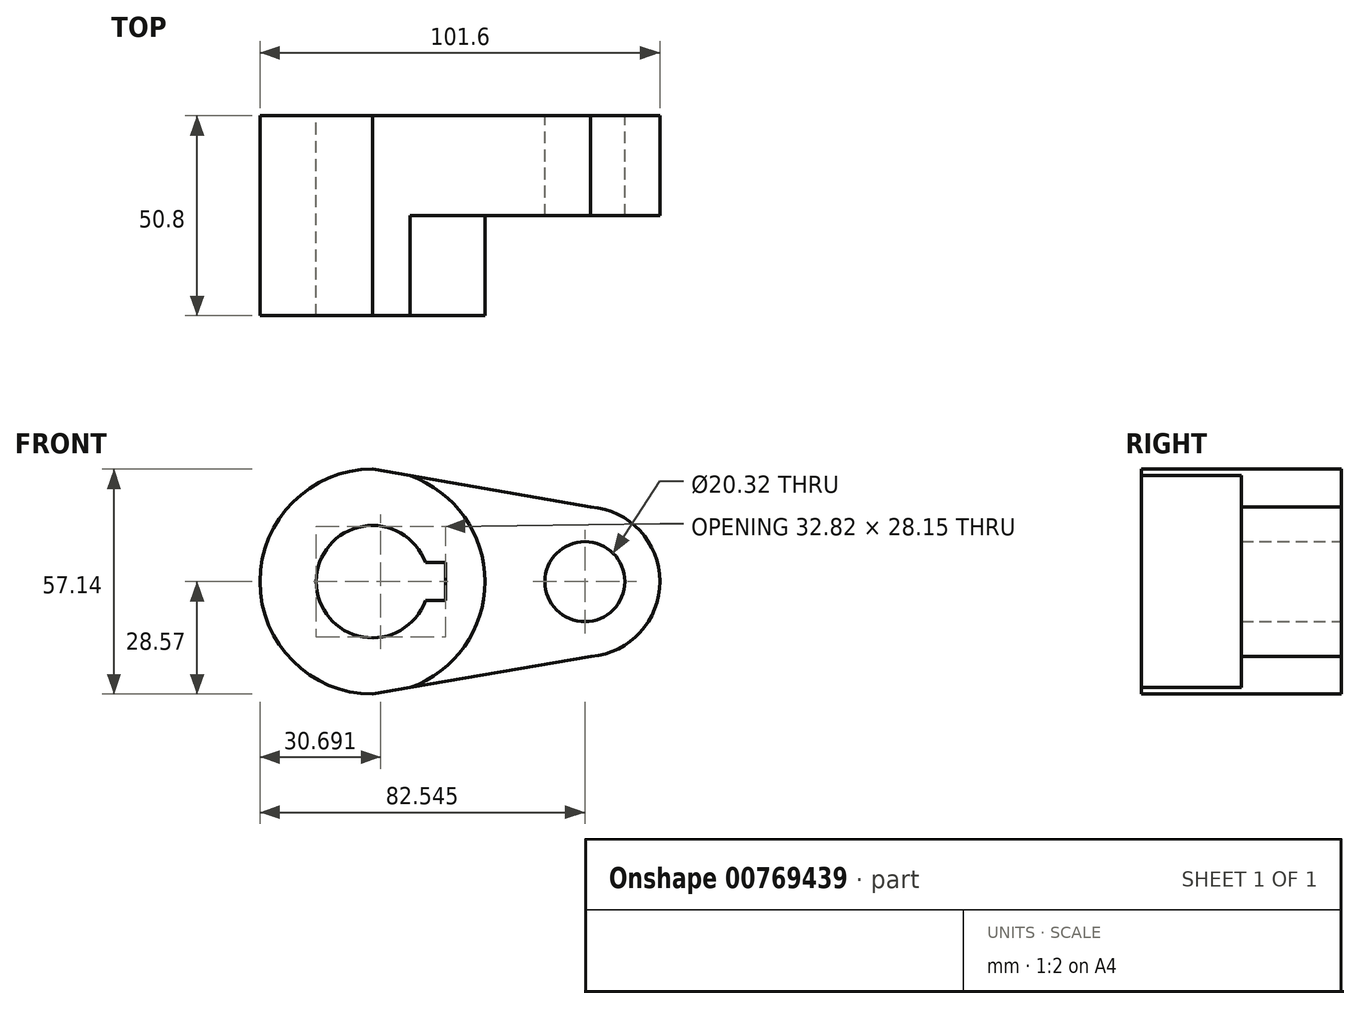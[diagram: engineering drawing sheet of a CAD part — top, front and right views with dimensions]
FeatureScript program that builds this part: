
annotation { "Feature Type Name" : "Feature", "Feature Type Description" : "" }
export const myFeature = defineFeature(function(context is Context, id is Id, definition is map)
    precondition{}
    {
        {
            var Q0;
            Q0=qCreatedBy(makeId("Front.planeOp"),FACE);
            var sketch = newSketch(context, id + "F0", { "sketchPlane" : qUnion([Q0])});
            skArc(sketch, "E0", {"start": v(0, 28.58) * mm, "mid": v(-28.58, 0) * mm, "end": v(0, -28.58) * mm});
            skArc(sketch, "E1", {"start": v(13.45, 4.83) * mm, "mid": v(-14.29, 0) * mm, "end": v(13.45, -4.83) * mm});
            skLineSegment(sketch, "E2.bottom", {"start": v(13.45, -4.83) * mm, "end": v(18.53, -4.83) * mm});
            skLineSegment(sketch, "E2.top", {"start": v(13.45, 4.83) * mm, "end": v(18.53, 4.83) * mm});
            skLineSegment(sketch, "E2.left", {"start": v(0, -4.83) * mm, "end": v(0, 0) * mm});
            skLineSegment(sketch, "E2.right", {"start": v(18.53, -4.83) * mm, "end": v(18.53, 4.83) * mm});
            skCircle(sketch, "E3", {"center": v(53.98, 0) * mm, "radius": 10.16 * mm});
            skCircle(sketch, "E4", {"center": v(53.98, 0) * mm, "radius": 19.05 * mm});
            skLineSegment(sketch, "E5", {"start": v(0, 28.58) * mm, "end": v(55.46, 19) * mm});
            skLineSegment(sketch, "E6", {"start": v(0, -28.58) * mm, "end": v(55.59, -18.98) * mm});
            skArc(sketch, "E7.trimOffspring", {"start": v(9.58, -26.92) * mm, "mid": v(28.57, 0) * mm, "end": v(9.59, 26.92) * mm});
            skPoint(sketch, "E8.orphan", {"position": v(0, 4.83) * mm});
            skSolve(sketch);
        }
        {
            var Q0;
            {var subQ1=sQuery(id+"F0.wireOp",EDGE,"E0");Q0=makeQuery(id+"F0.imprint","IMPRINT",FACE,{"disambiguationData":[TD([[makeQuery(id+"F0.imprint","IMPRINT",EDGE,{"derivedFrom":subQ1}),1.0]])]});}
            extrude(context, id + "F1", {"entities" : qUnion([Q0]), "depth" : 50.8 * mm, "offsetDistance" : 25.4 * mm});
        }
        {
            var Q0;
            Q0 = qSketchRegion(id + "F0", true);
            extrude(context, id + "F2", {"entities" : qUnion([Q0]), "operationType" : NewBodyOperationType.ADD, "depth" : 25.4 * mm, "offsetDistance" : 25.4 * mm});
        }
    });
